# Revit family: Reception-Teknion-B_CWL_Main_Worksurface_with_One_Gable_Reception_Desk-R2019
name_source: partatom
category: Furniture
units: mm (PartAtom-declared; Revit-internal decimal feet)

## family parameters
Always vertical = Yes
Cut with Voids When Loaded = No
OmniClass Number = 23.40.20.00
OmniClass Title = General Furniture and Specialties
Room Calculation Point = No
Shared = Yes
Work Plane-Based = No

## types (6) — shared parameters
Assembly Code = E2020200
Manufacturer = Teknion
Manufacturer Fax = 416.661.4586
Part Number = B_WCL
Product Documentation Link = https://www.teknion.com
Product Line = Expansion Casegoods
Product Page URL = https://www.teknion.com
Series = Expansion Casegoods
Sustainability Data = https://www.teknion.com
URL = www.teknion.com
Unit Weight URL = http://www.teknion.com
Warranty = http://www.teknion.com

## per-type parameters (varying)
| type | Description | Gable Thickness | Has Both Ends | Has Centered Rectangular Grommet | Model | Worksurface Thickness |
| 1" Thick WS, Centered Grommet | Main Worksurface with One Gable - Reception Desk, 1" Worksurface Thickness, Centered Grommet Option | 1.016 " | No | Yes | BDWCL____C_ | 1.016 " |
| 1-3/16" Thick WS, Centered Grommet | Main Worksurface with One Gable - Reception Desk, 1-3/16" Worksurface Thickness, Centered Grommet Option | 1.016 " | No | Yes | BMWCL____C_ | 1.189 " |
| 1-9/16" Thick WS, Centered Grommet | Main Worksurface with One Gable - Reception Desk, 1-9/16" Worksurface Thickness, Centered Grommet Option | 1.512 " | No | Yes | BXWCL____C_ | 1.555 " |
| 1" Thick WS, Both Ends Grommet | Main Worksurface with One Gable - Reception Desk, 1" Worksurface Thickness, Both Ends Grommet Option | 1.016 " | Yes | No | BDWCL____B_ | 1.016 " |
| 1-3/16" Thick WS, Both Ends Grommet | Main Worksurface with One Gable - Reception Desk, 1-3/16" Worksurface Thickness, Both Ends Grommet Option | 1.016 " | Yes | No | BMWCL____B_ | 1.189 " |
| 1-9/16" Thick WS, Both Ends Grommet | Main Worksurface with One Gable - Reception Desk, 1-9/16" Worksurface Thickness, Both Ends Grommet Option | 1.512 " | Yes | No | BXWCL____B_ | 1.555 " |

## geometry (parser evidence)
native form markers: Sweep x3
no freeform markers — native parametric forms only
